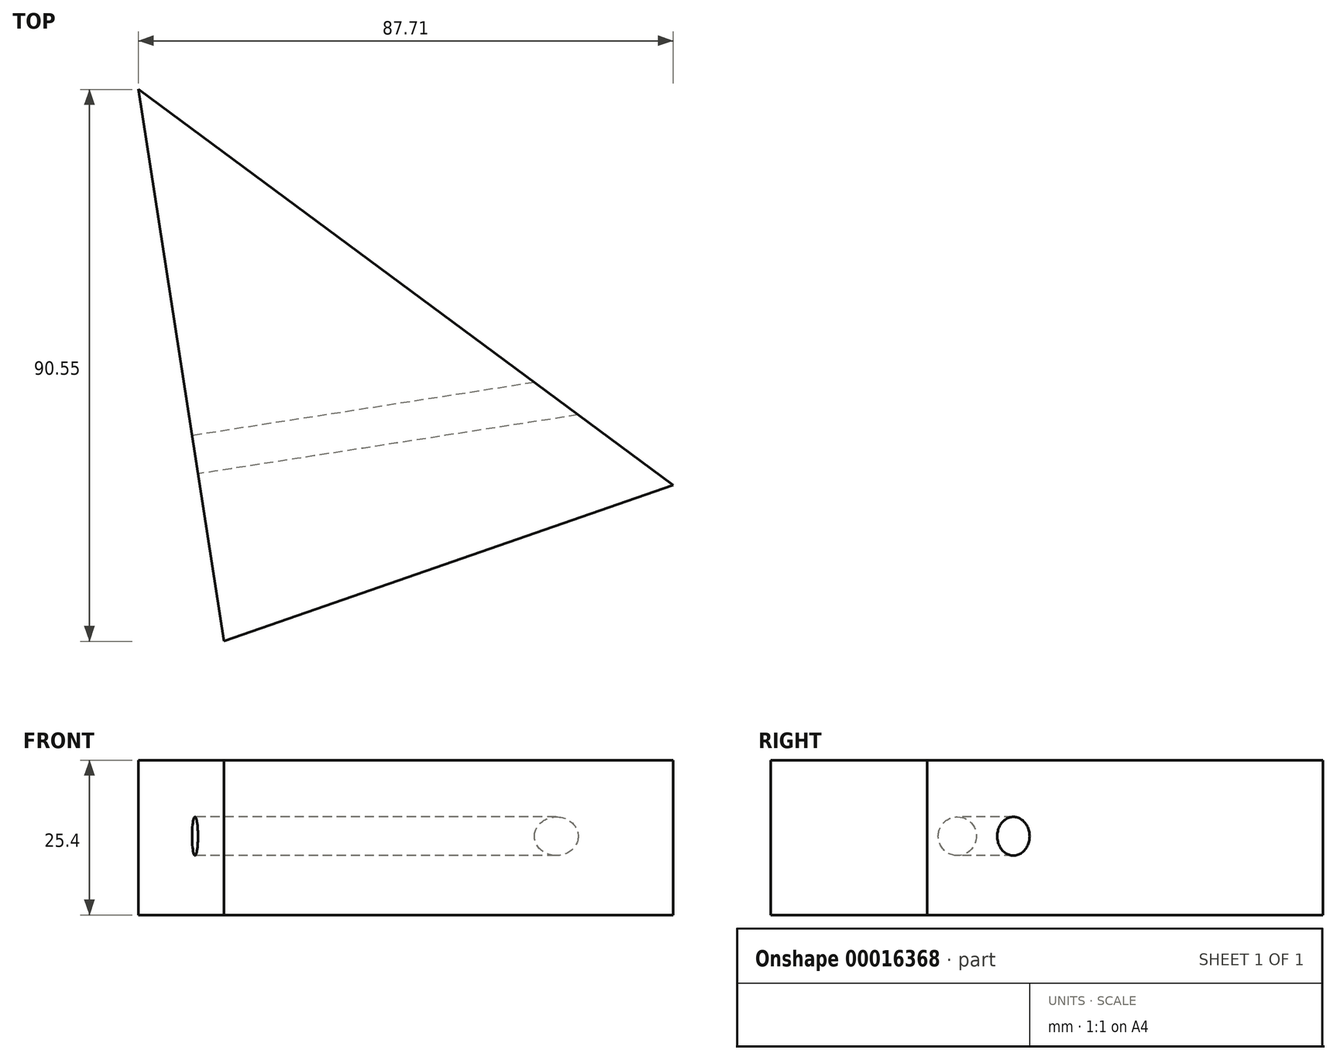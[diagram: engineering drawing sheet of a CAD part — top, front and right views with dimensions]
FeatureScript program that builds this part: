
annotation { "Feature Type Name" : "Feature", "Feature Type Description" : "" }
export const myFeature = defineFeature(function(context is Context, id is Id, definition is map)
    precondition{}
    {
        {
            var Q0;
            Q0=qCreatedBy(makeId("Top.planeOp"),FACE);
            var sketch = newSketch(context, id + "F0", { "sketchPlane" : qUnion([Q0])});
            skLineSegment(sketch, "E0", {"start": v(28.87, -12.67) * mm, "end": v(-44.78, -38.3) * mm});
            skLineSegment(sketch, "E1", {"start": v(-44.78, -38.3) * mm, "end": v(-58.84, 52.25) * mm});
            skLineSegment(sketch, "E2", {"start": v(-58.84, 52.25) * mm, "end": v(28.87, -12.67) * mm});
            skSolve(sketch);
        }
        {
            var Q0;
            Q0 = qSketchRegion(id + "F0", true);
            extrude(context, id + "F1", {"entities" : qUnion([Q0]), "depth" : 25.4 * mm});
        }
        {
            var Q0;
            Q0=makeQuery(id+"F1.opExtrude","SWEPT_FACE",FACE,{"disambiguationData":[OSD([sQuery(id+"F0.wireOp",EDGE,"E1")])]});
            var sketch = newSketch(context, id + "F2", { "sketchPlane" : qUnion([Q0])});
            skCircle(sketch, "E3", {"center": v(0, 12.91) * mm, "radius": 6.26 * mm});
            skSolve(sketch);
        }
        {
            var Q0;
            Q0=sQuery(id+"F2.wireOp",VERTEX,"E3.center");
            var Q1;
            Q1=makeQuery(id+"F1.opExtrude","SWEPT_BODY",BODY,{"disambiguationData":[OSD([sQuery(id+"F0.wireOp",EDGE,"E0"),sQuery(id+"F0.wireOp",EDGE,"E1"),sQuery(id+"F0.wireOp",EDGE,"E2")])]});
            hole(context, id + "F3", {"style" : HoleStyle.SIMPLE, "holeDiameter" : 6.35 * mm, "endStyle" : HoleEndStyle.THROUGH, "locations" : qUnion([Q0]), "scope" : qUnion([Q1])});
        }
    });
